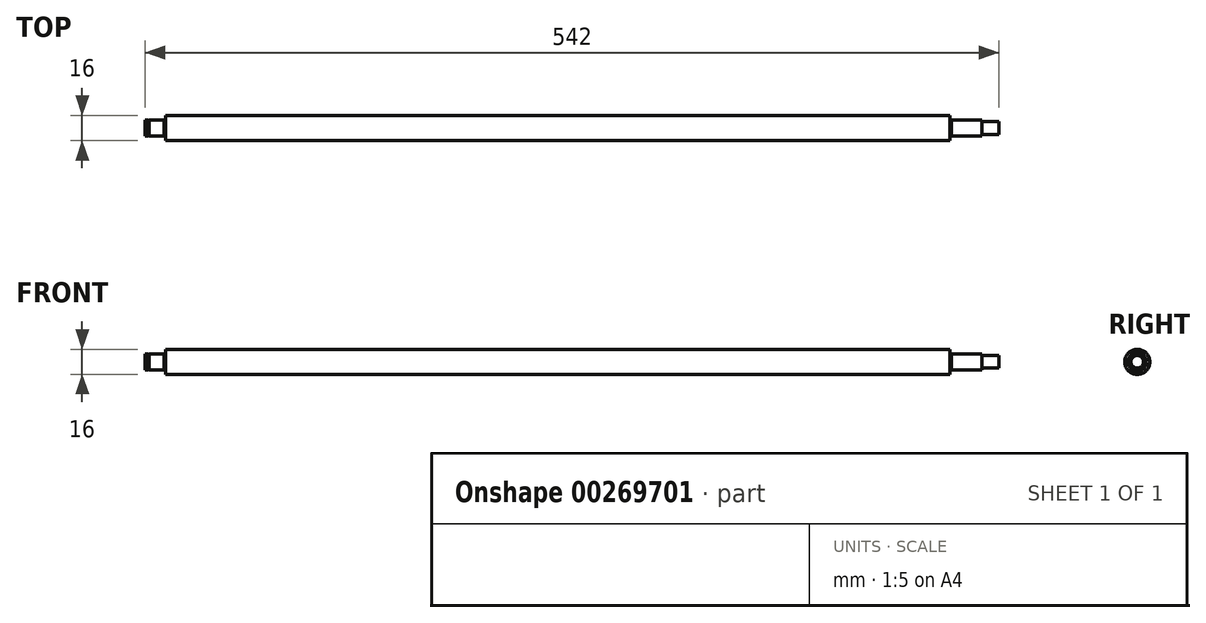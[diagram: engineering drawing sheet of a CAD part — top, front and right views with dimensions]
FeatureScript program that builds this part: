
annotation { "Feature Type Name" : "Feature", "Feature Type Description" : "" }
export const myFeature = defineFeature(function(context is Context, id is Id, definition is map)
    precondition{}
    {
        {
            var Q0;
            Q0=qCreatedBy(makeId("Front.planeOp"),FACE);
            var sketch = newSketch(context, id + "F0", { "sketchPlane" : qUnion([Q0])});
            skLineSegment(sketch, "E0", {"start": v(-263, 0) * mm, "end": v(279, 0) * mm});
            skLineSegment(sketch, "E1", {"start": v(279, 0) * mm, "end": v(279, 4) * mm});
            skLineSegment(sketch, "E2", {"start": v(279, 4) * mm, "end": v(268.5, 4) * mm});
            skLineSegment(sketch, "E3", {"start": v(268.5, 4) * mm, "end": v(268.5, 5) * mm});
            skLineSegment(sketch, "E4", {"start": v(268.5, 5) * mm, "end": v(249, 5) * mm});
            skLineSegment(sketch, "E5", {"start": v(249, 5) * mm, "end": v(249, 6) * mm});
            skLineSegment(sketch, "E6", {"start": v(249, 6) * mm, "end": v(248, 6) * mm});
            skLineSegment(sketch, "E7", {"start": v(248, 6) * mm, "end": v(248, 8) * mm});
            skLineSegment(sketch, "E8", {"start": v(248, 8) * mm, "end": v(-250, 8) * mm});
            skLineSegment(sketch, "E9", {"start": v(-250, 8) * mm, "end": v(-250, 6) * mm});
            skLineSegment(sketch, "E10", {"start": v(-250, 6) * mm, "end": v(-251, 6) * mm});
            skLineSegment(sketch, "E11", {"start": v(-251, 6) * mm, "end": v(-251, 5) * mm});
            skLineSegment(sketch, "E12", {"start": v(-251, 5) * mm, "end": v(-260.6, 5) * mm});
            skLineSegment(sketch, "E13", {"start": v(-260.6, 5) * mm, "end": v(-260.6, 4.8) * mm});
            skLineSegment(sketch, "E14", {"start": v(-260.6, 4.8) * mm, "end": v(-261.1, 4.8) * mm});
            skLineSegment(sketch, "E15", {"start": v(-261.1, 4.8) * mm, "end": v(-261.1, 5) * mm});
            skLineSegment(sketch, "E16", {"start": v(-261.1, 5) * mm, "end": v(-263, 5) * mm});
            skLineSegment(sketch, "E17", {"start": v(-263, 5) * mm, "end": v(-263, 0) * mm});
            skSolve(sketch);
        }
        {
            var Q0;
            Q0=makeQuery(id+"F0.imprint","IMPRINT",FACE,{"disambiguationData":[TD([[makeQuery(id+"F0.imprint","IMPRINT",EDGE,{"derivedFrom":sQuery(id+"F0.wireOp",EDGE,"E0")}),1.0]])]});
            var Q1;
            Q1=sQuery(id+"F0.wireOp",EDGE,"E0");
            revolve(context, id + "F1", {"entities" : qUnion([Q0]), "axis" : qUnion([Q1]), "revolveType" : RevolveType.FULL});
        }
    });
